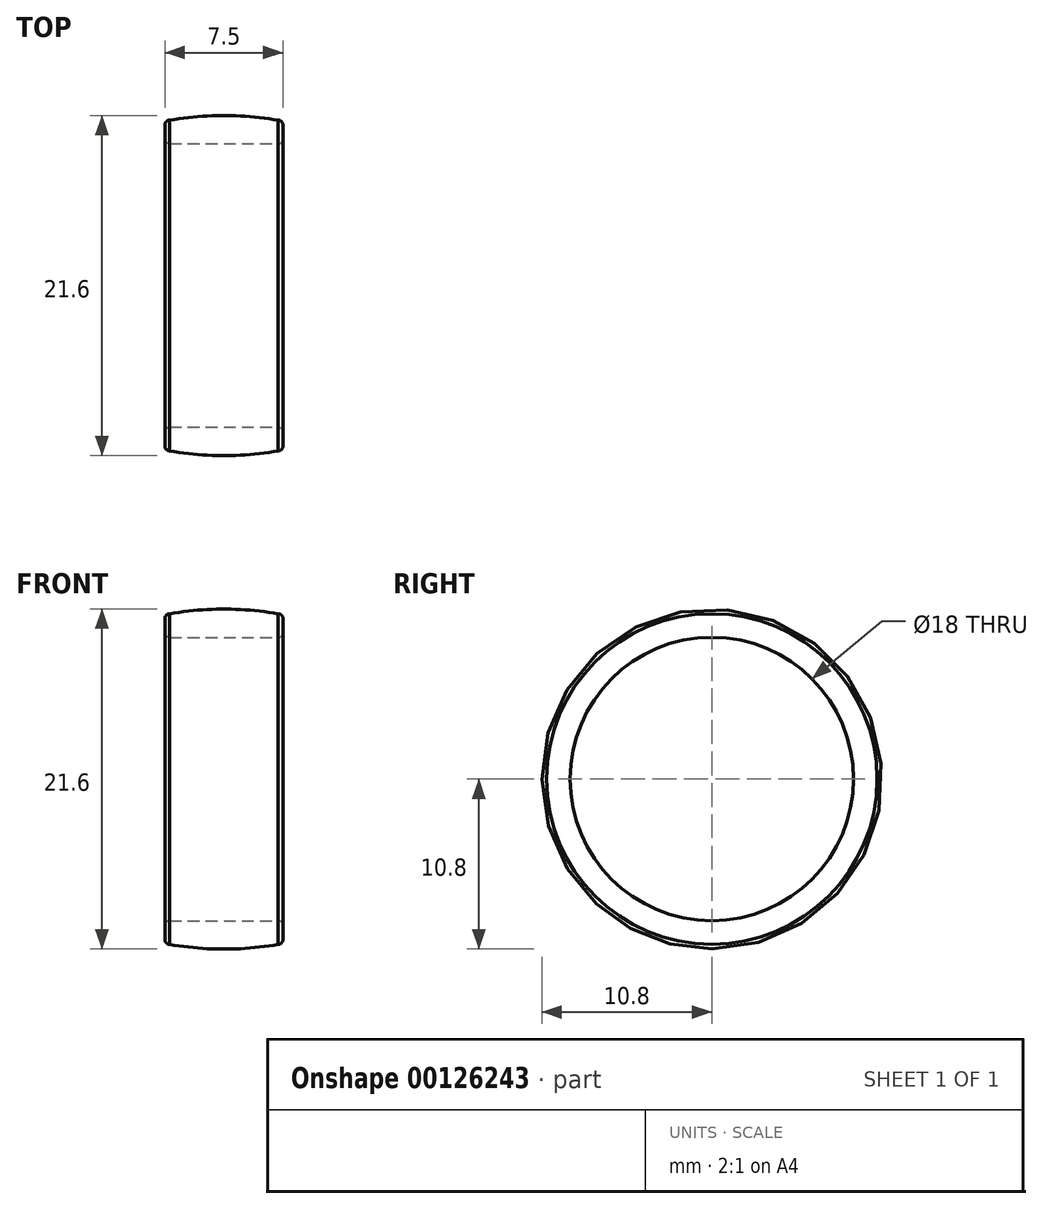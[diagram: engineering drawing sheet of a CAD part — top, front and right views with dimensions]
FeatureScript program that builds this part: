
annotation { "Feature Type Name" : "Feature", "Feature Type Description" : "" }
export const myFeature = defineFeature(function(context is Context, id is Id, definition is map)
    precondition{}
    {
        {
            var Q0;
            Q0=qCreatedBy(makeId("Front.planeOp"),FACE);
            var sketch = newSketch(context, id + "F0", { "sketchPlane" : qUnion([Q0])});
            skPoint(sketch, "E0.middle", {"position": v(-3.75, 9) * mm});
            skLineSegment(sketch, "E1.bottom", {"start": v(-3.45, 9) * mm, "end": v(3.45, 9) * mm});
            skLineSegment(sketch, "E1.top", {"start": v(-3.45, 10.5) * mm, "end": v(3.45, 10.5) * mm, "construction": true});
            skLineSegment(sketch, "E1.left", {"start": v(-3.75, 9.3) * mm, "end": v(-3.75, 10.2) * mm});
            skLineSegment(sketch, "E1.right", {"start": v(3.75, 9.3) * mm, "end": v(3.75, 10.2) * mm});
            skLineSegment(sketch, "E2", {"start": v(0, 0) * mm, "end": v(0, 9) * mm, "construction": true});
            skLineSegment(sketch, "E3", {"start": v(0, 0) * mm, "end": v(5, 0) * mm, "construction": true});
            skLineSegment(sketch, "E4", {"start": v(0, 9) * mm, "end": v(0, 10.5) * mm, "construction": true});
            skPoint(sketch, "E5.visualSharp", {"position": v(-3.75, 10.5) * mm});
            skArc(sketch, "E5.filletArc", {"start": v(-3.45, 10.5) * mm, "mid": v(-3.66, 10.41) * mm, "end": v(-3.75, 10.2) * mm});
            skArc(sketch, "E6.filletArc", {"start": v(-3.75, 9.3) * mm, "mid": v(-3.66, 9.09) * mm, "end": v(-3.45, 9) * mm});
            skPoint(sketch, "E7.visualSharp", {"position": v(3.75, 10.5) * mm});
            skArc(sketch, "E7.filletArc", {"start": v(3.75, 10.2) * mm, "mid": v(3.66, 10.41) * mm, "end": v(3.45, 10.5) * mm});
            skPoint(sketch, "E8.visualSharp", {"position": v(3.75, 9) * mm});
            skArc(sketch, "E8.filletArc", {"start": v(3.45, 9) * mm, "mid": v(3.66, 9.09) * mm, "end": v(3.75, 9.3) * mm});
            skArc(sketch, "E9", {"start": v(3.45, 10.5) * mm, "mid": v(0, 10.8) * mm, "end": v(-3.45, 10.5) * mm});
            skSolve(sketch);
        }
        {
            var Q0;
            Q0=makeQuery(id+"F0.imprint","IMPRINT",FACE,{"disambiguationData":[TD([[makeQuery(id+"F0.imprint","IMPRINT",EDGE,{"derivedFrom":sQuery(id+"F0.wireOp",EDGE,"E1.bottom")}),1.0]])]});
            var Q1;
            Q1=sQuery(id+"F0.wireOp",EDGE,"E3");
            revolve(context, id + "F1", {"entities" : qUnion([Q0]), "axis" : qUnion([Q1]), "revolveType" : RevolveType.FULL, "oppositeDirection" : true});
        }
    });
